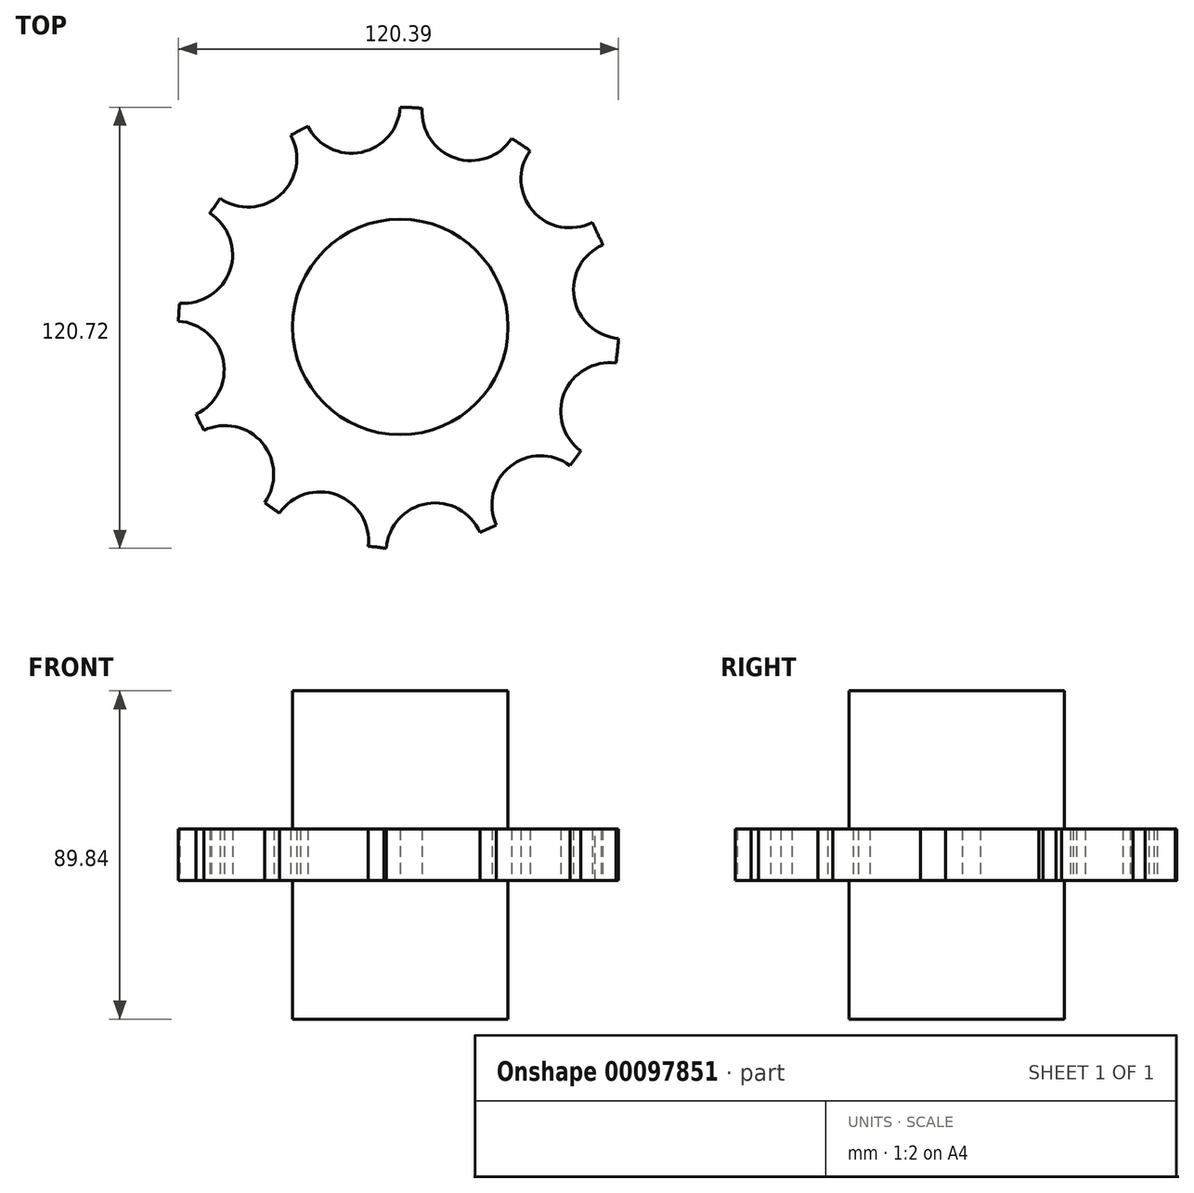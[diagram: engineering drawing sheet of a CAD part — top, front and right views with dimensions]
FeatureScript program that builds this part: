
annotation { "Feature Type Name" : "Feature", "Feature Type Description" : "" }
export const myFeature = defineFeature(function(context is Context, id is Id, definition is map)
    precondition{}
    {
        {
            var Q0;
            Q0=qCreatedBy(makeId("Top.planeOp"),FACE);
            var sketch = newSketch(context, id + "F0", { "sketchPlane" : qUnion([Q0])});
            skCircle(sketch, "E0", {"center": v(0, 0) * mm, "radius": 29.49 * mm});
            skCircle(sketch, "E1", {"center": v(0, 0) * mm, "radius": 48.83 * mm, "construction": true});
            skCircle(sketch, "E2", {"center": v(0, 0) * mm, "radius": 60.71 * mm});
            skArc(sketch, "E3", {"start": v(-25.38, 55.15) * mm, "mid": v(-10.49, 47.86) * mm, "end": v(0, 60.71) * mm});
            skArc(sketch, "E4.1.0", {"start": v(6.02, 60.04) * mm, "mid": v(15.14, 46.19) * mm, "end": v(30.7, 51.92) * mm});
            skCircle(sketch, "E4.1.1", {"center": v(-0.19, -0.35) * mm, "radius": 60.71 * mm});
            skArc(sketch, "E4.2.0", {"start": v(35.55, 48.27) * mm, "mid": v(36.35, 31.7) * mm, "end": v(52.66, 28.71) * mm});
            skCircle(sketch, "E4.2.1", {"center": v(-0.53, -0.56) * mm, "radius": 60.71 * mm});
            skPoint(sketch, "E4.center", {"position": v(-0.74, 0.17) * mm});
            skLineSegment(sketch, "E4.anchor1", {"start": v(-0.74, 0.17) * mm, "end": v(-25.38, 55.15) * mm, "construction": true});
            skLineSegment(sketch, "E4.anchor2", {"start": v(-0.74, 0.17) * mm, "end": v(35.55, 48.27) * mm, "construction": true});
            skArc(sketch, "E5.1.0", {"start": v(55.53, 22.5) * mm, "mid": v(47.6, 7.93) * mm, "end": v(59.97, -3.11) * mm});
            skArc(sketch, "E5.2.0", {"start": v(59.19, -9.92) * mm, "mid": v(44.83, -18.23) * mm, "end": v(49.67, -34.1) * mm});
            skPoint(sketch, "E5.center", {"position": v(-0.42, -0.23) * mm});
            skLineSegment(sketch, "E5.anchor1", {"start": v(-0.42, -0.23) * mm, "end": v(52.66, 28.71) * mm, "construction": true});
            skLineSegment(sketch, "E5.anchor2", {"start": v(-0.42, -0.23) * mm, "end": v(49.67, -34.1) * mm, "construction": true});
            skArc(sketch, "E6.1.0", {"start": v(46.62, -38.06) * mm, "mid": v(30.03, -38.22) * mm, "end": v(26.42, -54.41) * mm});
            skCircle(sketch, "E6.1.1", {"center": v(-0.74, -0.5) * mm, "radius": 60.71 * mm});
            skArc(sketch, "E6.2.0", {"start": v(21.83, -56.35) * mm, "mid": v(7.3, -48.33) * mm, "end": v(-3.8, -60.64) * mm});
            skCircle(sketch, "E6.2.1", {"center": v(-0.9, -0.34) * mm, "radius": 60.71 * mm, "construction": true});
            skArc(sketch, "E6.3.0", {"start": v(-8.76, -60.06) * mm, "mid": v(-17.44, -45.93) * mm, "end": v(-33.18, -51.17) * mm});
            skCircle(sketch, "E6.3.1", {"center": v(-0.95, -0.13) * mm, "radius": 60.71 * mm});
            skArc(sketch, "E6.4.0", {"start": v(-37.21, -48.23) * mm, "mid": v(-37.8, -31.65) * mm, "end": v(-54.08, -28.46) * mm});
            skCircle(sketch, "E6.4.1", {"center": v(-0.89, 0.09) * mm, "radius": 60.71 * mm});
            skPoint(sketch, "E6.center", {"position": v(-0.52, -0.13) * mm});
            skLineSegment(sketch, "E6.anchor1", {"start": v(-0.52, -0.13) * mm, "end": v(49.67, -34.1) * mm, "construction": true});
            skLineSegment(sketch, "E6.anchor2", {"start": v(-0.52, -0.13) * mm, "end": v(-54.08, -28.46) * mm, "construction": true});
            skArc(sketch, "E7.1.0", {"start": v(-56.1, -23.91) * mm, "mid": v(-48.43, -9.2) * mm, "end": v(-61.01, 1.6) * mm});
            skArc(sketch, "E7.2.0", {"start": v(-60.51, 6.55) * mm, "mid": v(-46.6, 15.57) * mm, "end": v(-52.2, 31.17) * mm});
            skArc(sketch, "E7.3.0", {"start": v(-49.33, 35.23) * mm, "mid": v(-32.77, 36.2) * mm, "end": v(-29.95, 52.55) * mm});
            skPoint(sketch, "E7.center", {"position": v(-0.58, -0.3) * mm});
            skLineSegment(sketch, "E7.anchor1", {"start": v(-0.58, -0.3) * mm, "end": v(-47.95, -40.31) * mm, "construction": true});
            skLineSegment(sketch, "E7.anchor2", {"start": v(-0.58, -0.3) * mm, "end": v(-41.66, 46.15) * mm, "construction": true});
            skFitSpline(sketch, "E8", {"points": [v(-37.21, -48.23) * mm, v(-47.95, -40.31) * mm, v(-54.08, -28.46) * mm, v(-56.1, -23.91) * mm, v(-61.53, -11.73) * mm, v(-61.01, 1.6) * mm, v(-60.51, 6.55) * mm, v(-59.23, 19.83) * mm, v(-52.2, 31.17) * mm, v(-49.33, 35.23) * mm, v(-41.66, 46.15) * mm, v(-29.95, 52.55) * mm, v(-25.38, 55.15) * mm, v(-13.34, 60.9) * mm, v(0, 60.71) * mm, v(6.02, 60.04) * mm, v(19.31, 58.86) * mm, v(30.7, 51.92) * mm, v(35.55, 48.27) * mm, v(46.4, 40.49) * mm, v(52.66, 28.71) * mm, v(55.53, 22.5) * mm, v(60.74, 10.2) * mm, v(59.97, -3.11) * mm, v(59.19, -9.92) * mm, v(57.25, -23.12) * mm, v(49.67, -34.1) * mm, v(46.62, -38.06) * mm, v(38.43, -48.59) * mm, v(26.42, -54.41) * mm, v(21.83, -56.35) * mm, v(9.51, -61.48) * mm, v(-3.8, -60.64) * mm, v(-8.76, -60.06) * mm, v(-22, -58.46) * mm, v(-33.18, -51.17) * mm, v(-37.21, -48.23) * mm]});
            skSolve(sketch);
        }
        {
            var Q0;
            Q0=makeQuery(id+"F0.imprint","IMPRINT",FACE,{"disambiguationData":[TD([[makeQuery(id+"F0.imprint","IMPRINT",EDGE,{"derivedFrom":sQuery(id+"F0.wireOp",EDGE,"E0")}),1.0]])]});
            extrude(context, id + "F1", {"entities" : qUnion([Q0]), "endBound" : BoundingType.SYMMETRIC, "depth" : 89.85 * mm});
        }
        {
            var Q0;
            Q0=makeQuery(id+"F0.imprint","IMPRINT",FACE,{"disambiguationData":[TD([[makeQuery(id+"F0.imprint","IMPRINT",EDGE,{"derivedFrom":sQuery(id+"F0.wireOp",EDGE,"E0")}),-1.0]])]});
            extrude(context, id + "F2", {"entities" : qUnion([Q0]), "operationType" : NewBodyOperationType.ADD, "endBound" : BoundingType.SYMMETRIC, "depth" : 14.08 * mm});
        }
    });
